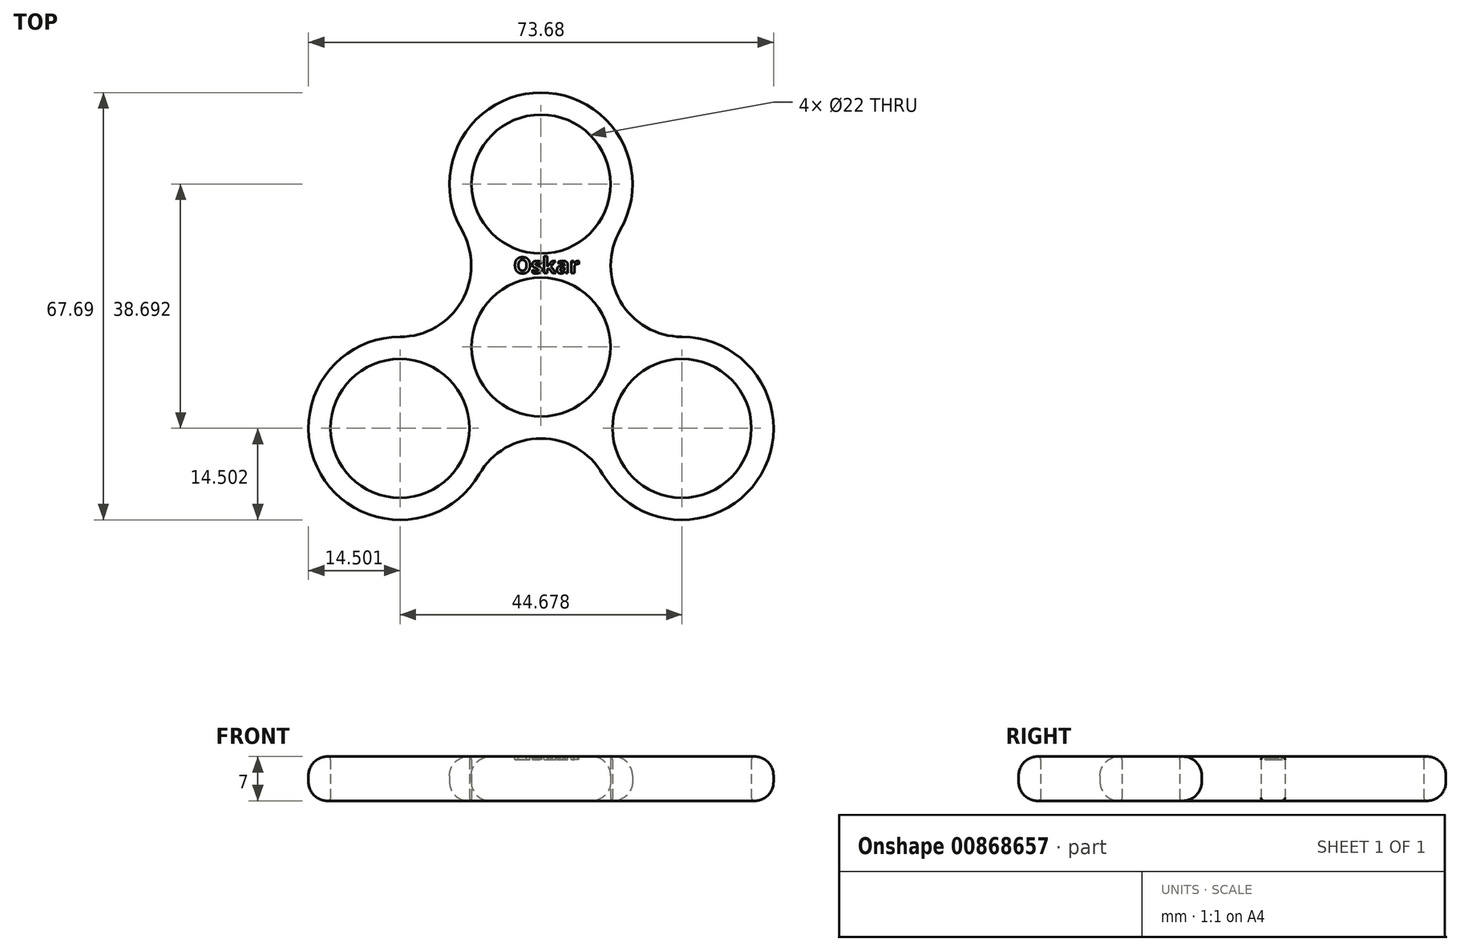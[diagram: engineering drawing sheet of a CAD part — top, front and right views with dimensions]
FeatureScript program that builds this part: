
annotation { "Feature Type Name" : "Feature", "Feature Type Description" : "" }
export const myFeature = defineFeature(function(context is Context, id is Id, definition is map)
    precondition{}
    {
        {
            var Q0;
            Q0=qCreatedBy(makeId("Top.planeOp"),FACE);
            var sketch = newSketch(context, id + "F0", { "sketchPlane" : qUnion([Q0])});
            skCircle(sketch, "E0", {"center": v(0, 0) * mm, "radius": 11 * mm});
            skCircle(sketch, "E1", {"center": v(0, 25.8) * mm, "radius": 11 * mm});
            skCircle(sketch, "E2", {"center": v(0, 25.8) * mm, "radius": 14.5 * mm, "construction": true});
            skLineSegment(sketch, "E3", {"start": v(0, 0) * mm, "end": v(-22.34, -12.9) * mm, "construction": true});
            skLineSegment(sketch, "E4", {"start": v(0, 0) * mm, "end": v(22.34, -12.9) * mm, "construction": true});
            skCircle(sketch, "E5", {"center": v(-22.34, -12.9) * mm, "radius": 14.5 * mm, "construction": true});
            skCircle(sketch, "E6", {"center": v(22.34, -12.9) * mm, "radius": 14.5 * mm, "construction": true});
            skCircle(sketch, "E7", {"center": v(0, 0) * mm, "radius": 40.3 * mm, "construction": true});
            skLineSegment(sketch, "E8.bottom", {"start": v(-40.3, -27.4) * mm, "end": v(40.3, -27.4) * mm, "construction": true});
            skLineSegment(sketch, "E8.top", {"start": v(-40.3, 40.3) * mm, "end": v(40.3, 40.3) * mm, "construction": true});
            skLineSegment(sketch, "E8.left", {"start": v(-40.3, -27.4) * mm, "end": v(-40.3, 40.3) * mm, "construction": true});
            skLineSegment(sketch, "E8.right", {"start": v(40.3, -27.4) * mm, "end": v(40.3, 40.3) * mm, "construction": true});
            skArc(sketch, "E9", {"start": v(12.56, 18.54) * mm, "mid": v(12.56, 7.25) * mm, "end": v(22.34, 1.6) * mm});
            skArc(sketch, "E10", {"start": v(12.56, 18.54) * mm, "mid": v(0, 40.3) * mm, "end": v(-12.56, 18.54) * mm});
            skLineSegment(sketch, "E11", {"start": v(12.56, 18.54) * mm, "end": v(-12.56, 18.54) * mm, "construction": true});
            skCircle(sketch, "E12.1.0", {"center": v(22.34, -12.9) * mm, "radius": 11 * mm});
            skArc(sketch, "E12.1.1", {"start": v(9.78, -20.15) * mm, "mid": v(0, -14.5) * mm, "end": v(-9.78, -20.15) * mm});
            skArc(sketch, "E12.1.2", {"start": v(9.78, -20.15) * mm, "mid": v(34.9, -20.15) * mm, "end": v(22.34, 1.6) * mm});
            skCircle(sketch, "E12.2.0", {"center": v(-22.34, -12.9) * mm, "radius": 11 * mm});
            skArc(sketch, "E12.2.1", {"start": v(-22.34, 1.6) * mm, "mid": v(-12.56, 7.25) * mm, "end": v(-12.56, 18.54) * mm});
            skArc(sketch, "E12.2.2", {"start": v(-22.34, 1.6) * mm, "mid": v(-34.9, -20.15) * mm, "end": v(-9.78, -20.15) * mm});
            skLineSegment(sketch, "E12.anchor1", {"start": v(0, 0) * mm, "end": v(0, 25.8) * mm, "construction": true});
            skLineSegment(sketch, "E13", {"start": v(0, 0) * mm, "end": v(-12.56, 7.25) * mm, "construction": true});
            skSolve(sketch);
        }
        {
            var Q0;
            Q0=makeQuery(id+"F0.imprint","IMPRINT",FACE,{"disambiguationData":[TD([[makeQuery(id+"F0.imprint","IMPRINT",EDGE,{"derivedFrom":sQuery(id+"F0.wireOp",EDGE,"E0")}),-1.0]])]});
            extrude(context, id + "F1", {"entities" : qUnion([Q0]), "depth" : 7 * mm, "offsetDistance" : 25.4 * mm});
        }
        {
            var Q0;
            Q0=makeQuery(id+"F1.opExtrude","CAP_EDGE",EDGE,{"disambiguationData":[OSD([sQuery(id+"F0.wireOp",EDGE,"E12.1.1")])],"isStart":false});
            var Q1;
            Q1=makeQuery(id+"F1.opExtrude","SWEPT_FACE",FACE,{"disambiguationData":[OSD([sQuery(id+"F0.wireOp",EDGE,"E12.1.1")])]});
            fillet(context, id + "F2", {"entities" : qUnion([Q0, Q1]), "radius" : 3 * mm, "tangentPropagation" : true, "allowEdgeOverflow" : false});
        }
        {
            var Q0;
            Q0=makeQuery(id+"F1.opExtrude","CAP_EDGE",EDGE,{"disambiguationData":[OSD([sQuery(id+"F0.wireOp",EDGE,"E0")])],"isStart":true});
            var Q1;
            Q1=makeQuery(id+"F1.opExtrude","CAP_EDGE",EDGE,{"disambiguationData":[OSD([sQuery(id+"F0.wireOp",EDGE,"E0")])],"isStart":false});
            var Q2;
            Q2=makeQuery(id+"F1.opExtrude","CAP_EDGE",EDGE,{"disambiguationData":[OSD([sQuery(id+"F0.wireOp",EDGE,"E1")])],"isStart":false});
            var Q3;
            Q3=makeQuery(id+"F1.opExtrude","CAP_EDGE",EDGE,{"disambiguationData":[OSD([sQuery(id+"F0.wireOp",EDGE,"E1")])],"isStart":true});
            var Q4;
            Q4=makeQuery(id+"F1.opExtrude","CAP_EDGE",EDGE,{"disambiguationData":[OSD([sQuery(id+"F0.wireOp",EDGE,"E12.1.0")])],"isStart":false});
            var Q5;
            Q5=makeQuery(id+"F1.opExtrude","CAP_EDGE",EDGE,{"disambiguationData":[OSD([sQuery(id+"F0.wireOp",EDGE,"E12.1.0")])],"isStart":true});
            var Q6;
            Q6=makeQuery(id+"F1.opExtrude","CAP_EDGE",EDGE,{"disambiguationData":[OSD([sQuery(id+"F0.wireOp",EDGE,"E12.2.0")])],"isStart":false});
            var Q7;
            Q7=makeQuery(id+"F1.opExtrude","CAP_EDGE",EDGE,{"disambiguationData":[OSD([sQuery(id+"F0.wireOp",EDGE,"E12.2.0")])],"isStart":true});
            fillet(context, id + "F3", {"entities" : qUnion([Q0, Q1, Q2, Q3, Q4, Q5, Q6, Q7]), "radius" : 0.5 * mm, "tangentPropagation" : true, "allowEdgeOverflow" : false});
        }
        {
            var Q0;
            Q0=makeQuery(id+"F3.opFillet","SPLIT",FACE,{"disambiguationData":[OD(2.0)],"derivedFrom":makeQuery(id+"F1.opExtrude","CAP_FACE",FACE,{"disambiguationData":[OSD([sQuery(id+"F0.wireOp",EDGE,"E0"),sQuery(id+"F0.wireOp",EDGE,"E1"),sQuery(id+"F0.wireOp",EDGE,"E9"),sQuery(id+"F0.wireOp",EDGE,"E10"),sQuery(id+"F0.wireOp",EDGE,"E12.1.0"),sQuery(id+"F0.wireOp",EDGE,"E12.1.1"),sQuery(id+"F0.wireOp",EDGE,"E12.1.2"),sQuery(id+"F0.wireOp",EDGE,"E12.2.0"),sQuery(id+"F0.wireOp",EDGE,"E12.2.1"),sQuery(id+"F0.wireOp",EDGE,"E12.2.2")])],"isStart":false})});
            var sketch = newSketch(context, id + "F4", { "sketchPlane" : qUnion([Q0])});
            skText(sketch, "E14", { "text": "Oskar", "fontName": "OpenSans-Bold.ttf"});
            const initialGuessF4  = {"E14": [-0.00433, 0.01168, 1, 0, 0.00253]};
            skSetInitialGuess(sketch, initialGuessF4);
            skSolve(sketch);
        }
        {
            var Q0;
            Q0 = qSketchRegion(id + "F4", true);
            extrude(context, id + "F5", {"entities" : qUnion([Q0]), "operationType" : NewBodyOperationType.REMOVE, "oppositeDirection" : true, "depth" : 0.5 * mm, "offsetDistance" : 25 * mm});
        }
    });
